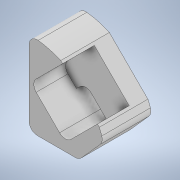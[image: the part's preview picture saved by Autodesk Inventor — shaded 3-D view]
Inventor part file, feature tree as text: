
AUTODESK INVENTOR PART (.ipt)
format: ipt  version: 2020 (Build 240168000, 168)  size: 150,016 bytes
history: native  units: in
note: dims shown in document units (in); Inventor stores cm internally (conversion verified against a paired STEP export)
features: extrude x3, sketch x3, direct_edit x1, fillet x1, move_body x1
ambient origin geometry x8: Origin, YZ Plane, XZ Plane, XY Plane, X Axis, Y Axis, Z Axis, Center Point
bodies: Solid1 (feature_tree)
feature tree (9):
  extrude  "Extrusion1"  Depth=0.3in
  extrude  "Extrusion2"  Depth=0.4865in
  direct_edit  "Direct Edit1"
  extrude  "Extrusion3"  Depth=0.76in
  fillet  "Fillet1"  Radius=0.49in
  sketch  "Sketch1"  dims[d0=2.972in d1=0.3in]
  sketch  "Sketch2"  dims[d2=0.84in d3=0.4865in]
  sketch  "Sketch3"  dims[d4=0.75in d5=0.0in d6=0.76in d7=0.49in d8=0.04in d9=0.7in d10=0.0in d11=0.0in d12=0.0in d13=0.1in d14=0.45in d15=0.2in d16=0.75in d17=0.0in d18=0.125in]
  move_body  "Move1"
